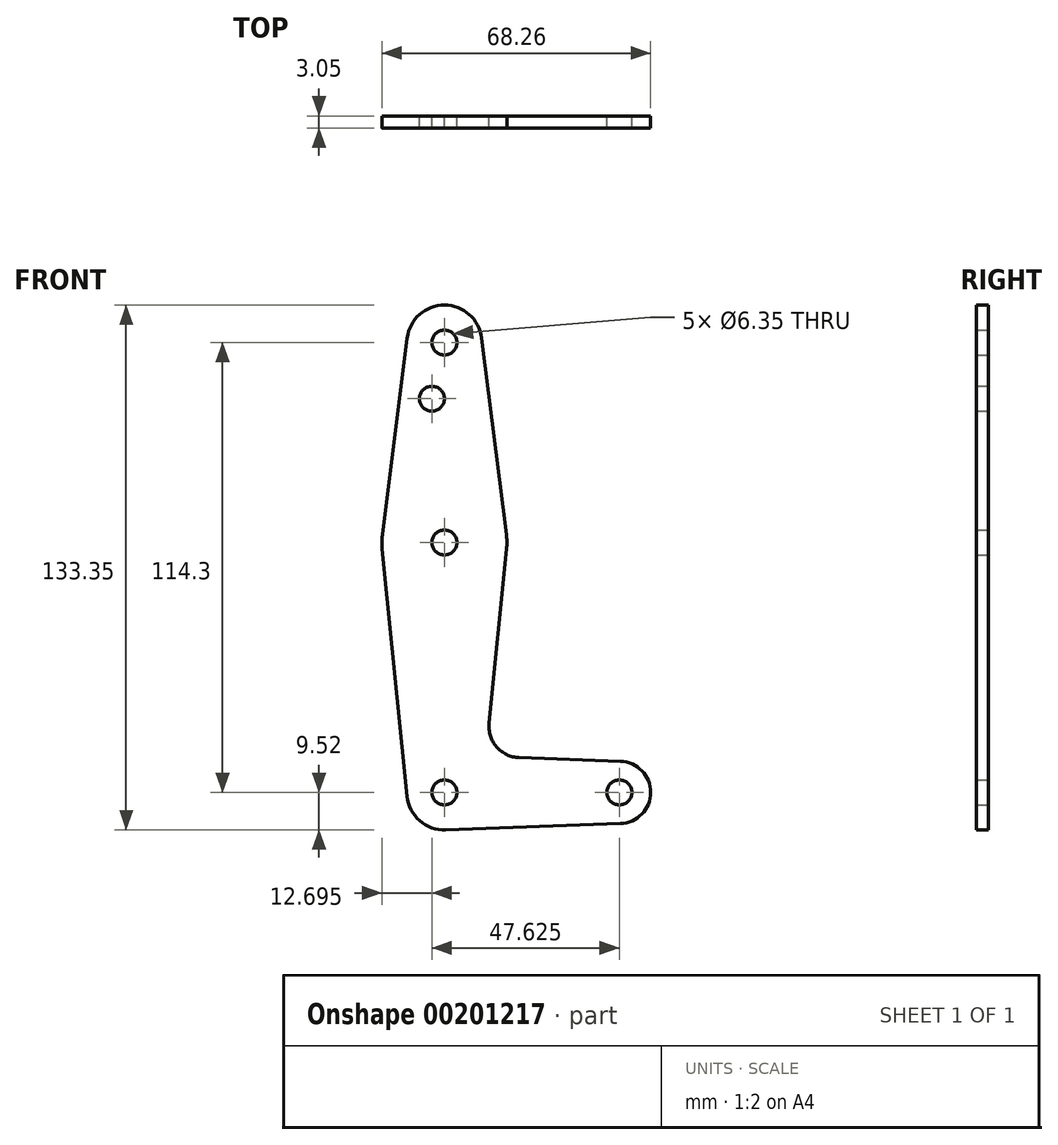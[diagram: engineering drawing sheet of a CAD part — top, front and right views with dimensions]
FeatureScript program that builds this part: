
annotation { "Feature Type Name" : "Feature", "Feature Type Description" : "" }
export const myFeature = defineFeature(function(context is Context, id is Id, definition is map)
    precondition{}
    {
        {
            var Q0;
            Q0=qCreatedBy(makeId("Front.planeOp"),FACE);
            var sketch = newSketch(context, id + "F0", { "sketchPlane" : qUnion([Q0])});
            skCircle(sketch, "E0", {"center": v(0, 0) * mm, "radius": 9.53 * mm});
            skCircle(sketch, "E1", {"center": v(0, 63.5) * mm, "radius": 15.88 * mm});
            skCircle(sketch, "E2", {"center": v(0, 114.3) * mm, "radius": 9.53 * mm});
            skCircle(sketch, "E3", {"center": v(44.45, 0) * mm, "radius": 7.94 * mm});
            skLineSegment(sketch, "E4", {"start": v(-9.45, 115.5) * mm, "end": v(-15.75, 65.48) * mm});
            skLineSegment(sketch, "E5", {"start": v(9.45, 115.5) * mm, "end": v(15.75, 65.48) * mm});
            skLineSegment(sketch, "E6", {"start": v(-15.8, 61.91) * mm, "end": v(-9.48, -0.95) * mm});
            skLineSegment(sketch, "E7", {"start": v(15.8, 61.91) * mm, "end": v(11.34, 17.6) * mm});
            skLineSegment(sketch, "E8", {"start": v(18.97, 8.85) * mm, "end": v(44.73, 7.93) * mm});
            skLineSegment(sketch, "E9", {"start": v(0.34, -9.52) * mm, "end": v(44.73, -7.93) * mm});
            skCircle(sketch, "E10", {"center": v(-3.17, 100.03) * mm, "radius": 3.18 * mm});
            skCircle(sketch, "E11", {"center": v(0, 114.3) * mm, "radius": 3.18 * mm});
            skCircle(sketch, "E12", {"center": v(0, 63.5) * mm, "radius": 3.18 * mm});
            skCircle(sketch, "E13", {"center": v(0, 0) * mm, "radius": 3.18 * mm});
            skCircle(sketch, "E14", {"center": v(44.45, 0) * mm, "radius": 3.18 * mm});
            skArc(sketch, "E15.filletArc", {"start": v(11.34, 17.6) * mm, "mid": v(13.26, 11.57) * mm, "end": v(18.97, 8.85) * mm});
            skSolve(sketch);
        }
        {
            var Q0;
            Q0=makeQuery(id+"F0.imprint","IMPRINT",FACE,{"disambiguationData":[TD([[makeQuery(id+"F0.imprint","IMPRINT",EDGE,{"derivedFrom":sQuery(id+"F0.wireOp",EDGE,"E11")}),-1.0]])]});
            var Q1;
            {var subQ1=sQuery(id+"F0.wireOp",EDGE,"E4");Q1=makeQuery(id+"F0.imprint","IMPRINT",FACE,{"disambiguationData":[TD([[makeQuery(id+"F0.imprint","IMPRINT",EDGE,{"derivedFrom":subQ1}),1.0]])]});}
            var Q2;
            Q2=makeQuery(id+"F0.imprint","IMPRINT",FACE,{"disambiguationData":[TD([[makeQuery(id+"F0.imprint","IMPRINT",EDGE,{"derivedFrom":sQuery(id+"F0.wireOp",EDGE,"E12")}),-1.0]])]});
            var Q3;
            {var subQ0=sQuery(id+"F0.wireOp",EDGE,"E6");Q3=makeQuery(id+"F0.imprint","IMPRINT",FACE,{"disambiguationData":[TD([[makeQuery(id+"F0.imprint","IMPRINT",EDGE,{"derivedFrom":subQ0}),1.0]])]});}
            var Q4;
            Q4=makeQuery(id+"F0.imprint","IMPRINT",FACE,{"disambiguationData":[TD([[makeQuery(id+"F0.imprint","IMPRINT",EDGE,{"derivedFrom":sQuery(id+"F0.wireOp",EDGE,"E14")}),-1.0]])]});
            var Q5;
            Q5=makeQuery(id+"F0.imprint","IMPRINT",FACE,{"disambiguationData":[TD([[makeQuery(id+"F0.imprint","IMPRINT",EDGE,{"derivedFrom":sQuery(id+"F0.wireOp",EDGE,"E13")}),-1.0]])]});
            extrude(context, id + "F1", {"entities" : qUnion([Q0, Q1, Q2, Q3, Q4, Q5]), "depth" : 3.05 * mm});
        }
    });
